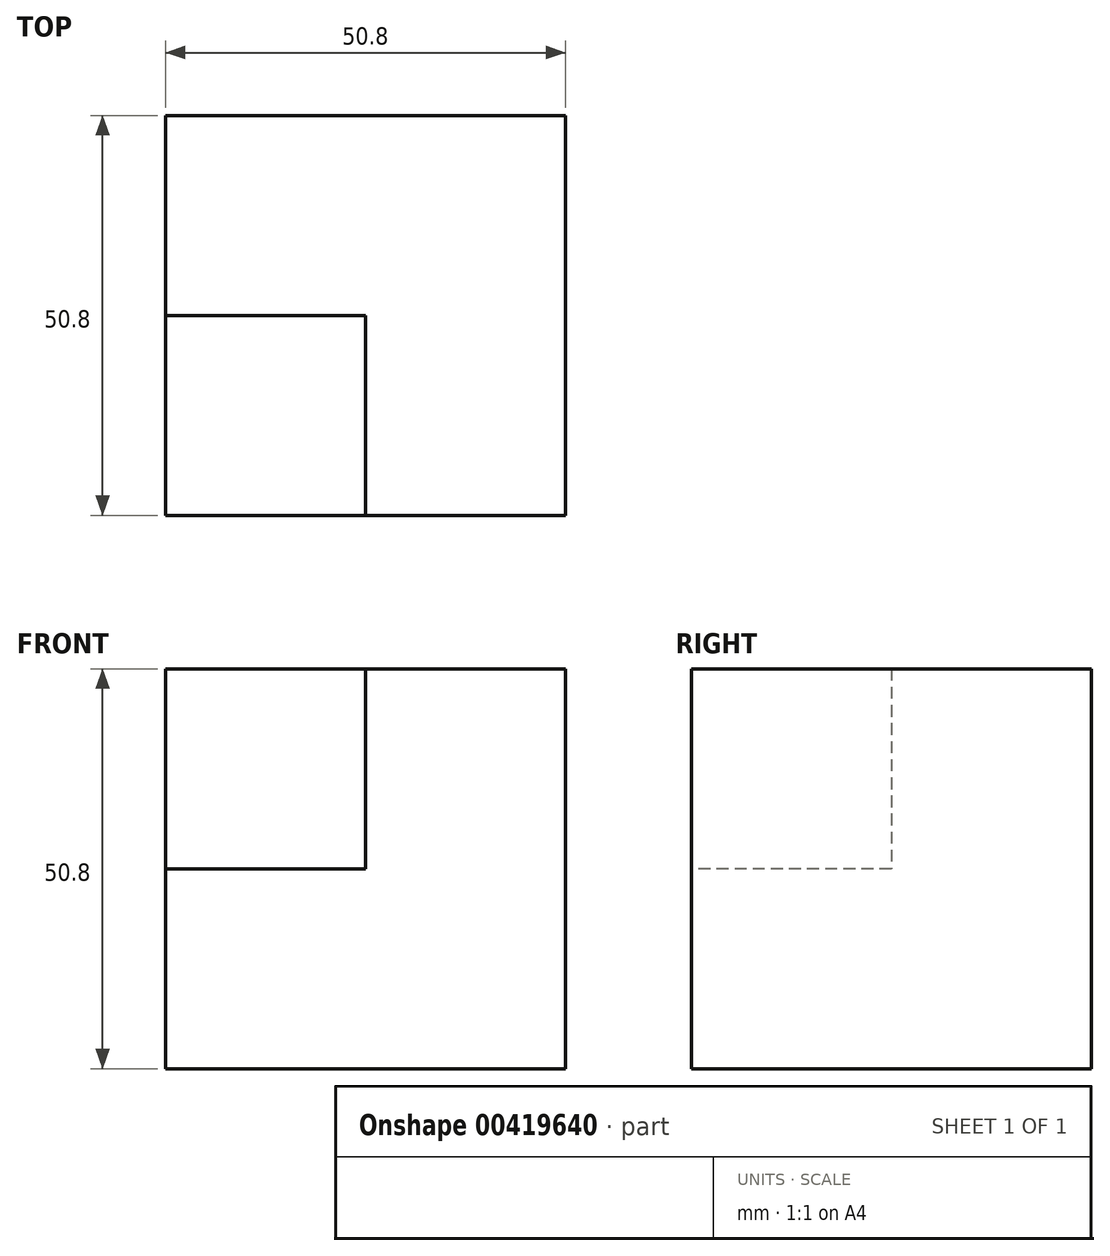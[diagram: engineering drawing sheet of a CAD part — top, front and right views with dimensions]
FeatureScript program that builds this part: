
annotation { "Feature Type Name" : "Feature", "Feature Type Description" : "" }
export const myFeature = defineFeature(function(context is Context, id is Id, definition is map)
    precondition{}
    {
        {
            var Q0;
            Q0=qCreatedBy(makeId("Front.planeOp"),FACE);
            var sketch = newSketch(context, id + "F0", { "sketchPlane" : qUnion([Q0])});
            skLineSegment(sketch, "E0.bottom", {"start": v(0, 0) * mm, "end": v(50.8, 0) * mm});
            skLineSegment(sketch, "E0.top", {"start": v(0, -50.8) * mm, "end": v(50.8, -50.8) * mm});
            skLineSegment(sketch, "E0.left", {"start": v(0, 0) * mm, "end": v(0, -50.8) * mm});
            skLineSegment(sketch, "E0.right", {"start": v(50.8, 0) * mm, "end": v(50.8, -50.8) * mm});
            skSolve(sketch);
        }
        {
            var Q0;
            Q0=makeQuery(id+"F0.imprint","IMPRINT",FACE,{"disambiguationData":[TD([[makeQuery(id+"F0.imprint","IMPRINT",EDGE,{"derivedFrom":sQuery(id+"F0.wireOp",EDGE,"E0.bottom")}),-1.0]])]});
            extrude(context, id + "F1", {"entities" : qUnion([Q0]), "depth" : 25.4 * mm});
        }
        {
            var Q0;
            Q0=makeQuery(id+"F1.opExtrude","CAP_FACE",FACE,{"disambiguationData":[OSD([sQuery(id+"F0.wireOp",EDGE,"E0.bottom"),sQuery(id+"F0.wireOp",EDGE,"E0.top"),sQuery(id+"F0.wireOp",EDGE,"E0.left"),sQuery(id+"F0.wireOp",EDGE,"E0.right")])],"isStart":false});
            extrude(context, id + "F2", {"entities" : qUnion([Q0]), "operationType" : NewBodyOperationType.ADD, "depth" : 25.4 * mm});
        }
        {
            var Q0;
            Q0=makeQuery(id+"F2.opExtrude","CAP_FACE",FACE,{"disambiguationData":[OSD([sQuery(id+"F0.wireOp",EDGE,"E0.bottom"),sQuery(id+"F0.wireOp",EDGE,"E0.top"),sQuery(id+"F0.wireOp",EDGE,"E0.left"),sQuery(id+"F0.wireOp",EDGE,"E0.right")])],"isStart":false});
            var sketch = newSketch(context, id + "F3", { "sketchPlane" : qUnion([Q0])});
            skLineSegment(sketch, "E1.bottom", {"start": v(0, 0) * mm, "end": v(25.4, 0) * mm});
            skLineSegment(sketch, "E1.top", {"start": v(0, -25.4) * mm, "end": v(25.4, -25.4) * mm});
            skLineSegment(sketch, "E1.left", {"start": v(0, 0) * mm, "end": v(0, -25.4) * mm});
            skLineSegment(sketch, "E1.right", {"start": v(25.4, 0) * mm, "end": v(25.4, -25.4) * mm});
            skSolve(sketch);
        }
        {
            var Q0;
            Q0 = qSketchRegion(id + "F3", true);
            var Q1;
            Q1=makeQuery(id+"F3.imprint","IMPRINT",FACE,{"disambiguationData":[TD([[makeQuery(id+"F3.imprint","IMPRINT",EDGE,{"derivedFrom":sQuery(id+"F3.wireOp",EDGE,"E1.bottom")}),-1.0]])]});
            extrude(context, id + "F4", {"entities" : qUnion([Q0, Q1]), "operationType" : NewBodyOperationType.REMOVE, "oppositeDirection" : true, "depth" : 25.4 * mm});
        }
    });
